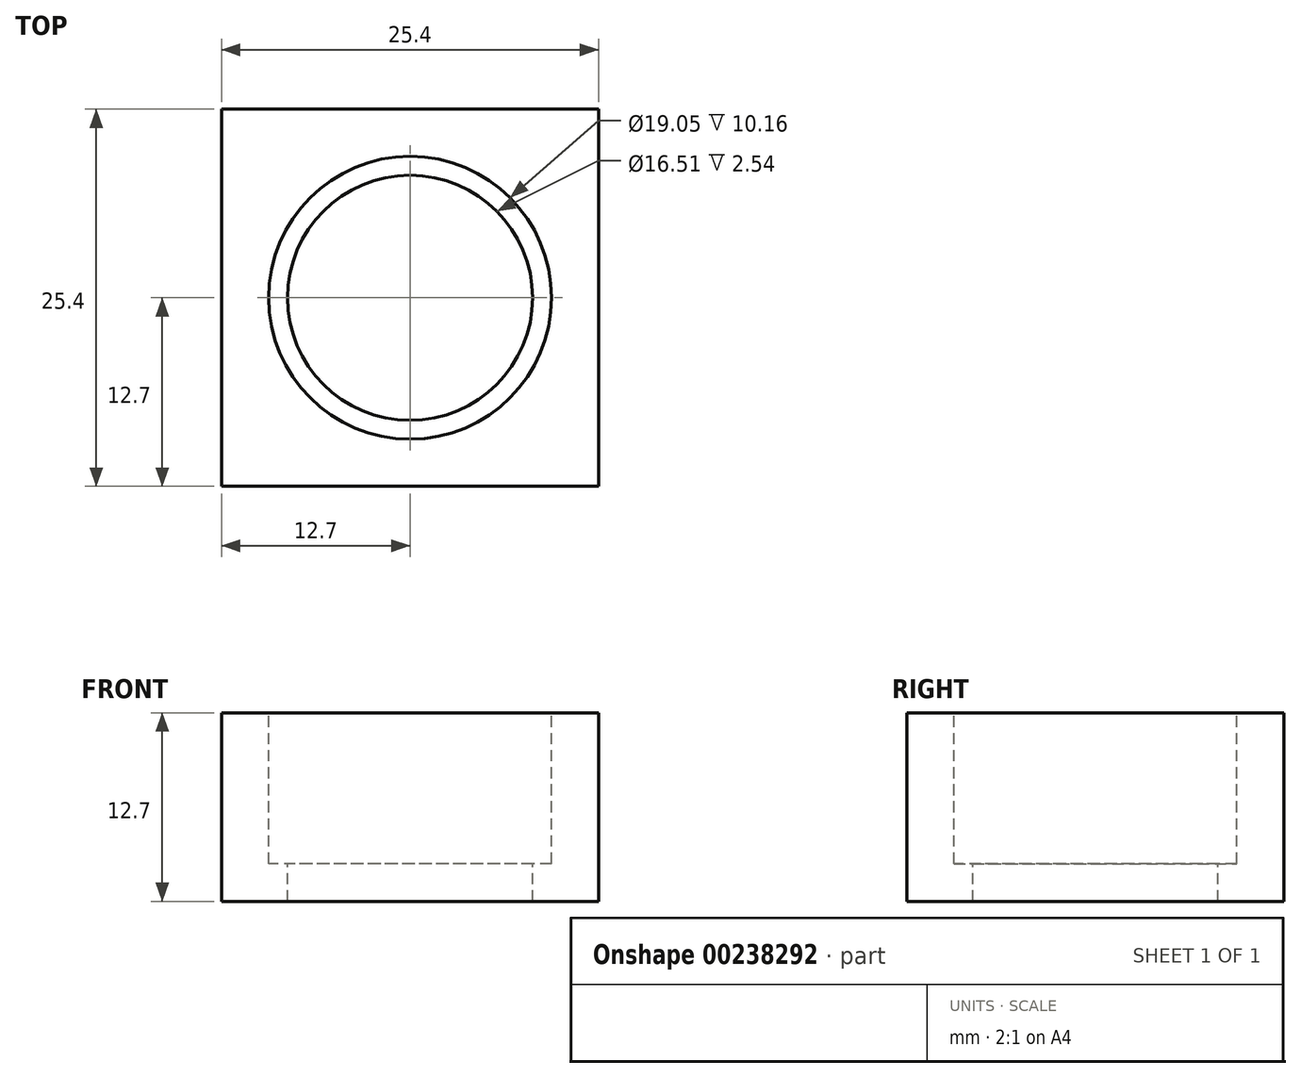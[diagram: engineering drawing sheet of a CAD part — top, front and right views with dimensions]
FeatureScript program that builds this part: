
annotation { "Feature Type Name" : "Feature", "Feature Type Description" : "" }
export const myFeature = defineFeature(function(context is Context, id is Id, definition is map)
    precondition{}
    {
        {
            var Q0;
            Q0=qCreatedBy(makeId("Top.planeOp"),FACE);
            var sketch = newSketch(context, id + "F0", { "sketchPlane" : qUnion([Q0])});
            skLineSegment(sketch, "E0.bottom", {"start": v(0, 0) * mm, "end": v(25.4, 0) * mm});
            skLineSegment(sketch, "E0.top", {"start": v(0, 25.4) * mm, "end": v(25.4, 25.4) * mm});
            skLineSegment(sketch, "E0.left", {"start": v(0, 0) * mm, "end": v(0, 25.4) * mm});
            skLineSegment(sketch, "E0.right", {"start": v(25.4, 0) * mm, "end": v(25.4, 25.4) * mm});
            skSolve(sketch);
        }
        {
            var Q0;
            Q0=makeQuery(id+"F0.imprint","IMPRINT",FACE,{"disambiguationData":[TD([[makeQuery(id+"F0.imprint","IMPRINT",EDGE,{"derivedFrom":sQuery(id+"F0.wireOp",EDGE,"E0.bottom")}),1.0]])]});
            extrude(context, id + "F1", {"entities" : qUnion([Q0]), "depth" : 12.7 * mm});
        }
        {
            var Q0;
            Q0=makeQuery(id+"F1.opExtrude","CAP_FACE",FACE,{"disambiguationData":[OSD([sQuery(id+"F0.wireOp",EDGE,"E0.bottom"),sQuery(id+"F0.wireOp",EDGE,"E0.top"),sQuery(id+"F0.wireOp",EDGE,"E0.left"),sQuery(id+"F0.wireOp",EDGE,"E0.right")])],"isStart":false});
            var sketch = newSketch(context, id + "F2", { "sketchPlane" : qUnion([Q0])});
            skCircle(sketch, "E1", {"center": v(12.7, 12.7) * mm, "radius": 9.53 * mm});
            skPoint(sketch, "E1.centerSnap0", {"position": v(0, 12.7) * mm});
            skPoint(sketch, "E1.centerSnap1", {"position": v(12.7, 25.4) * mm});
            skSolve(sketch);
        }
        {
            var Q0;
            Q0 = qSketchRegion(id + "F2", true);
            extrude(context, id + "F3", {"entities" : qUnion([Q0]), "operationType" : NewBodyOperationType.REMOVE, "oppositeDirection" : true, "depth" : 10.16 * mm});
        }
        {
            var Q0;
            Q0=makeQuery(id+"F3.boolean.opBoolean","COPY",FACE,{"derivedFrom":makeQuery(id+"F3.opExtrude","CAP_FACE",FACE,{"disambiguationData":[OSD([sQuery(id+"F2.wireOp",EDGE,"E1")])],"isStart":false})});
            var sketch = newSketch(context, id + "F4", { "sketchPlane" : qUnion([Q0])});
            skCircle(sketch, "E2", {"center": v(12.7, 12.7) * mm, "radius": 8.26 * mm});
            skSolve(sketch);
        }
        {
            var Q0;
            Q0=makeQuery(id+"F4.imprint","IMPRINT",FACE,{"disambiguationData":[TD([[makeQuery(id+"F4.imprint","IMPRINT",EDGE,{"derivedFrom":sQuery(id+"F4.wireOp",EDGE,"E2")}),1.0]])]});
            extrude(context, id + "F5", {"entities" : qUnion([Q0]), "operationType" : NewBodyOperationType.REMOVE, "endBound" : BoundingType.THROUGH_ALL, "oppositeDirection" : true, "depth" : 25.4 * mm});
        }
    });
